# Revit family: Drinking_Fountain-Haws_Corporation-Pedestal_3202
name_source: partatom
category: Plumbing Fixtures
revit_build: Autodesk Revit Architecture 2014 (Build: 20131024_2115(x64)
units: mm (PartAtom-declared; Revit-internal decimal feet)

## types (2) — shared parameters
Assembly Code = D2010810
Bowl Height = 27"
CWFU = 1
Cost = $0.00
Cost Note = For Cost information please visit the Resource tab in the Product Page URL
Description = Barrier-Free Pedestal Fountain
Flow = 0.00 GPM
Full Length = 30 3/8"
HW Connection = No
HWFU = 1
Keynote = 15410.A1
Manufacturer = Haws Corporation 1455 Kleppe Lane Sparks, NV 89431
Product Documentation Link = https://www.hawsco.com
Product Page URL = https://www.hawsco.com
Series = Barrier-Free Steel Pedestal Fountain
Supply Radius = 1/4"
To Spot Outlet = 33 1/2"
Type Comments = Trough style 12 gauge galvanized steel pedestal drinking fountain.
URL = http://www.hawsco.com
Vent Connection = No
WFU = 1
Waste Connection = Yes
Width = 10"

## per-type parameters (varying)
| type | Pedestal |
| 3202G | Metal - Haws Corporation - Galvanized Steel |
| 3202 | Metal - Haws Corporation - Green Powder Coated Finish |

note: column(s) folded — value = type name in every type: Model

## geometry (parser evidence)
native form markers: Blend x16, Sweep x5
no freeform markers — native parametric forms only
